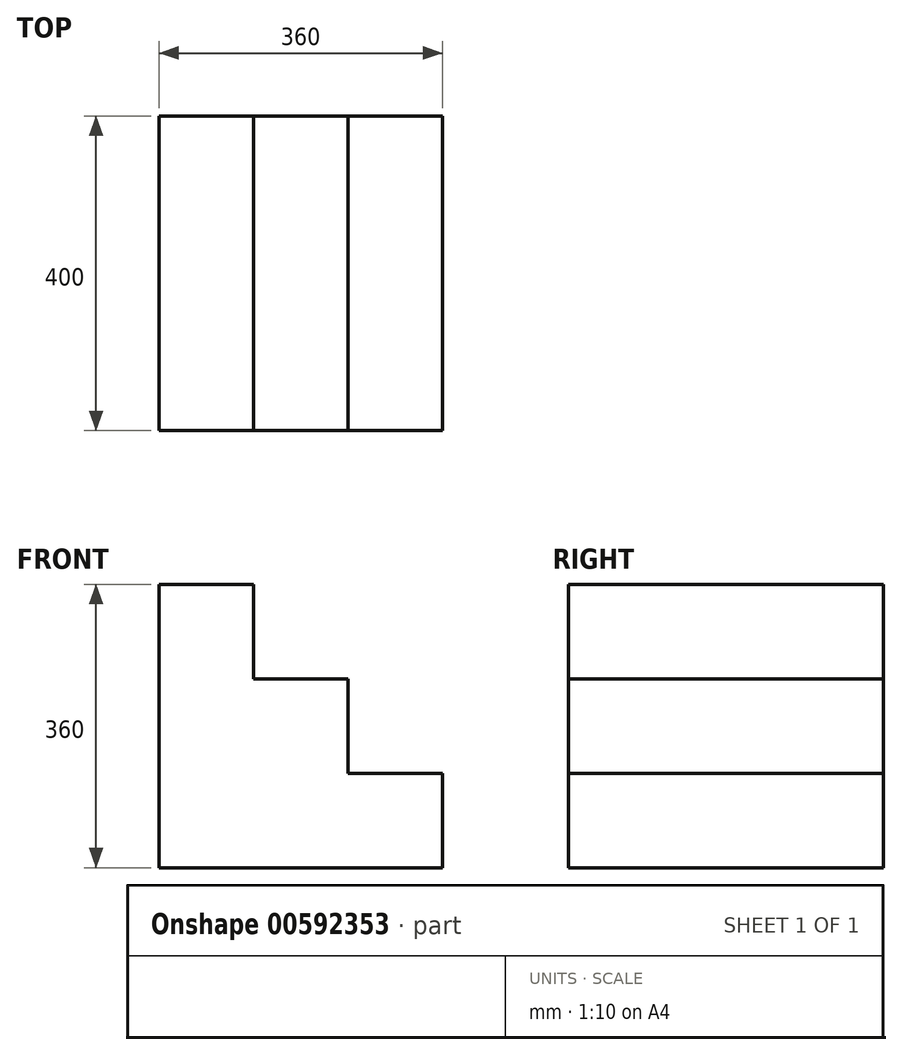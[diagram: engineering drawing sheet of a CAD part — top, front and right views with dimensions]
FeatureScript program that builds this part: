
annotation { "Feature Type Name" : "Feature", "Feature Type Description" : "" }
export const myFeature = defineFeature(function(context is Context, id is Id, definition is map)
    precondition{}
    {
        {
            var Q0;
            Q0=qCreatedBy(makeId("Front.planeOp"),FACE);
            var sketch = newSketch(context, id + "F0", { "sketchPlane" : qUnion([Q0])});
            skLineSegment(sketch, "E0", {"start": v(0, 0) * mm, "end": v(360, 0) * mm});
            skLineSegment(sketch, "E1", {"start": v(0, 0) * mm, "end": v(0, 360) * mm});
            skLineSegment(sketch, "E2", {"start": v(0, 360) * mm, "end": v(120, 360) * mm});
            skLineSegment(sketch, "E3", {"start": v(120, 360) * mm, "end": v(120, 240) * mm});
            skLineSegment(sketch, "E4", {"start": v(120, 240) * mm, "end": v(240, 240) * mm});
            skLineSegment(sketch, "E5", {"start": v(240, 240) * mm, "end": v(240, 120) * mm});
            skLineSegment(sketch, "E6", {"start": v(240, 120) * mm, "end": v(360, 120) * mm});
            skLineSegment(sketch, "E7", {"start": v(360, 120) * mm, "end": v(360, 0) * mm});
            skSolve(sketch);
        }
        {
            var Q0;
            Q0 = qSketchRegion(id + "F0", true);
            extrude(context, id + "F1", {"entities" : qUnion([Q0]), "depth" : 400 * mm, "offsetDistance" : 25 * mm});
        }
    });
